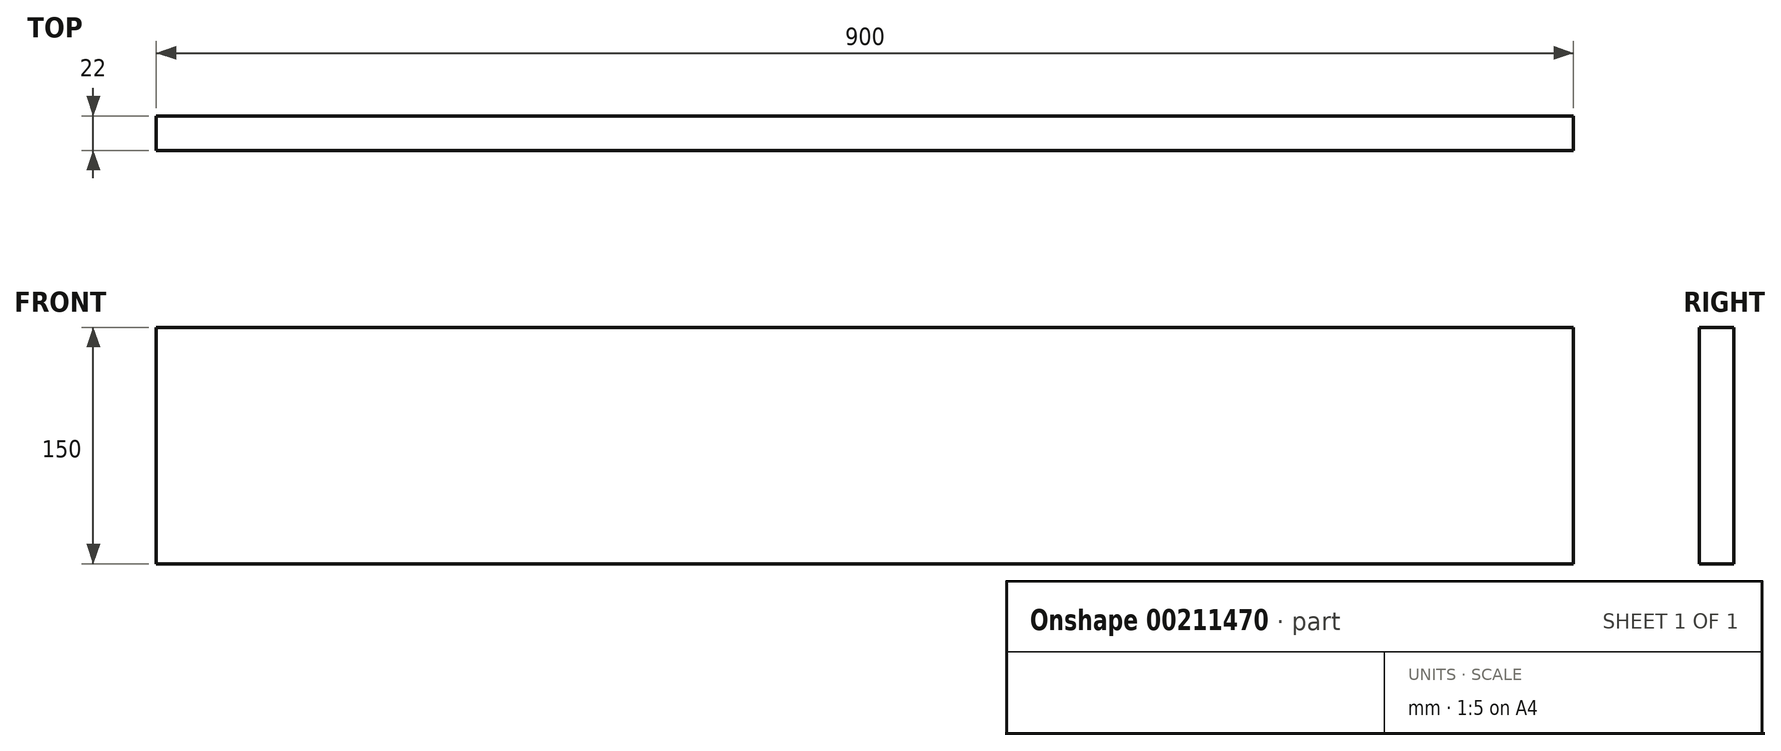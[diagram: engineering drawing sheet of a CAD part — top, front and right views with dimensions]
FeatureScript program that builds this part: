
annotation { "Feature Type Name" : "Feature", "Feature Type Description" : "" }
export const myFeature = defineFeature(function(context is Context, id is Id, definition is map)
    precondition{}
    {
        {
            var Q0;
            Q0=qCreatedBy(makeId("Front.planeOp"),FACE);
            var sketch = newSketch(context, id + "F0", { "sketchPlane" : qUnion([Q0])});
            skLineSegment(sketch, "E0.bottom", {"start": v(-450, 75) * mm, "end": v(450, 75) * mm});
            skLineSegment(sketch, "E0.top", {"start": v(-450, -75) * mm, "end": v(450, -75) * mm});
            skLineSegment(sketch, "E0.left", {"start": v(-450, 75) * mm, "end": v(-450, -75) * mm});
            skLineSegment(sketch, "E0.right", {"start": v(450, 75) * mm, "end": v(450, -75) * mm});
            skSolve(sketch);
        }
        {
            var Q0;
            Q0=qSketchRegion(id+"F0",true);
            extrude(context, id + "F1", {"entities" : qUnion([Q0]), "depth" : 22 * mm});
        }
    });
